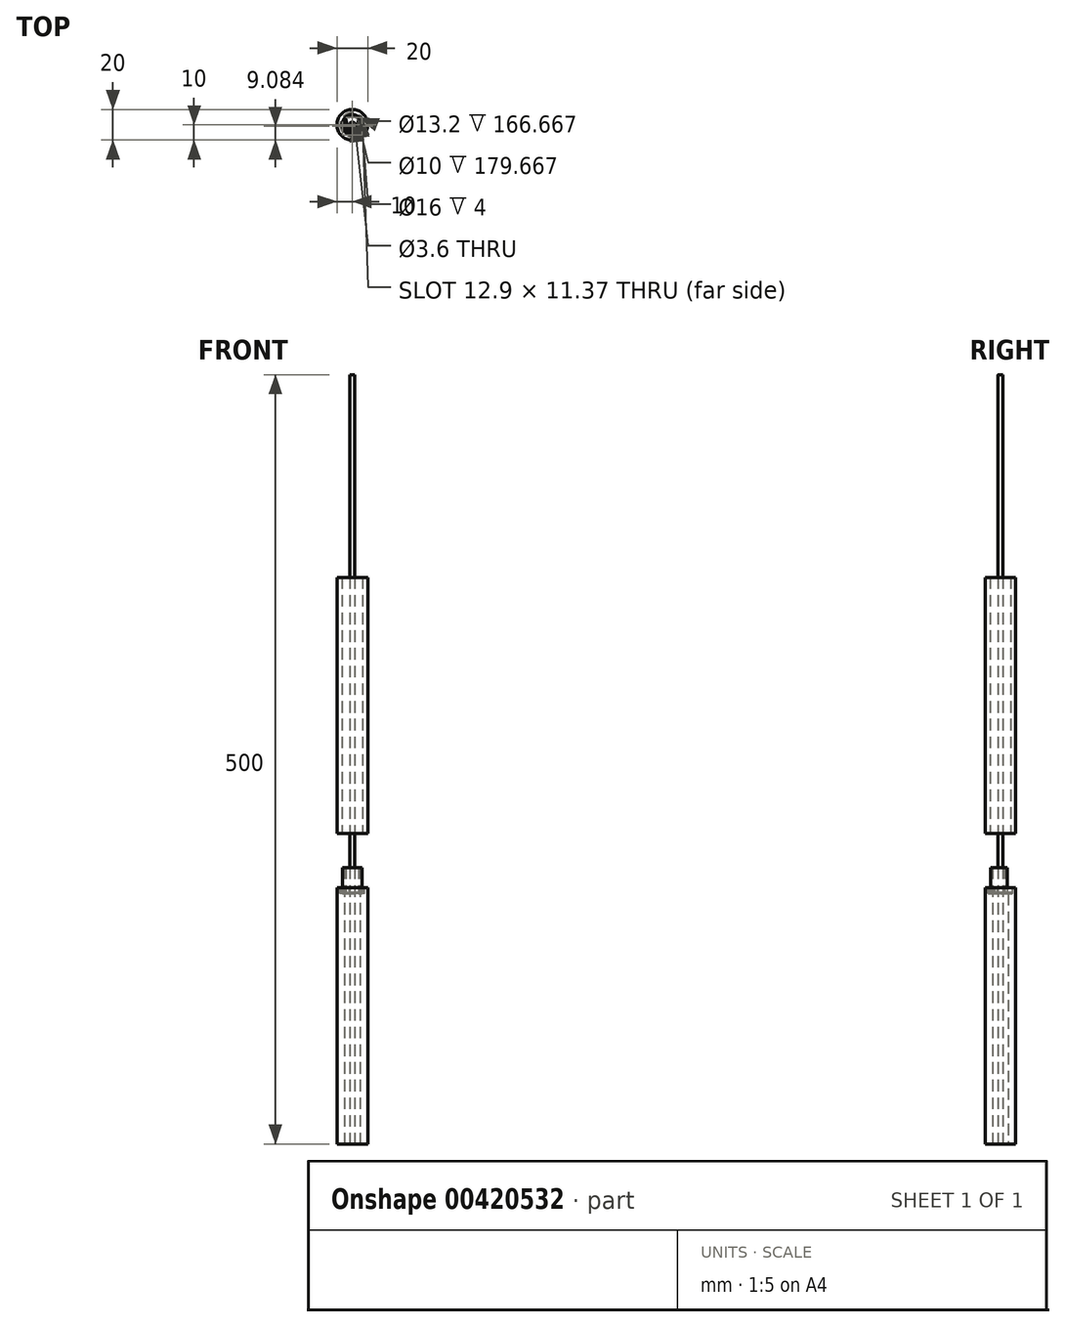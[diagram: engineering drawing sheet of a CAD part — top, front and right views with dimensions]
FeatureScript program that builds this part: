
annotation { "Feature Type Name" : "Feature", "Feature Type Description" : "" }
export const myFeature = defineFeature(function(context is Context, id is Id, definition is map)
    precondition{}
    {
        {
            assignVariable(context, id + "F0", {"name" : "RodLength", "anyValue" : 500 * mm});
        }
        {
            assignVariable(context, id + "F1", {"name" : "NubDepth", "anyValue" : 13 * mm});
        }
        {
            assignVariable(context, id + "F2", {"name" : "EjectorSupportRingDepth", "anyValue" : 3.2 * mm});
        }
        {
            var Q0;
            Q0=qCreatedBy(makeId("Top.planeOp"),FACE);
            cPlane(context, id + "F3", {"entities" : qUnion([Q0]), "cplaneType" : CPlaneType.OFFSET, "offset" : getVariable(context, 'RodLength') / 3, "width" : 150 * mm, "height" : 150 * mm});
        }
        {
            var Q0;
            Q0=qCreatedBy(id+"F3.planeOp",FACE);
            var sketch = newSketch(context, id + "F4", { "sketchPlane" : qUnion([Q0])});
            skArc(sketch, "E0", {"start": v(-4.56, 4.77) * mm, "mid": v(0, -6.6) * mm, "end": v(4.56, 4.77) * mm});
            skCircle(sketch, "E1", {"center": v(0, 0) * mm, "radius": 7.8 * mm});
            skCircle(sketch, "E2", {"center": v(0, 0) * mm, "radius": 1.8 * mm});
            skArc(sketch, "E3", {"start": v(-3.32, -0.75) * mm, "mid": v(0, -3.4) * mm, "end": v(3.32, -0.75) * mm});
            skLineSegment(sketch, "E4", {"start": v(-7.1, -0.75) * mm, "end": v(6.56, -0.75) * mm, "construction": true});
            skLineSegment(sketch, "E5", {"start": v(-3.32, -0.75) * mm, "end": v(-4.56, 4.77) * mm});
            skLineSegment(sketch, "E6", {"start": v(3.32, -0.75) * mm, "end": v(4.56, 4.77) * mm});
            skArc(sketch, "E7", {"start": v(-4.12, 2.83) * mm, "mid": v(0, -5) * mm, "end": v(4.12, 2.83) * mm});
            skPoint(sketch, "E8", {"position": v(-4.12, 2.83) * mm});
            skLineSegment(sketch, "E9", {"start": v(-4.12, 2.83) * mm, "end": v(-4.12, -8.26) * mm, "construction": true});
            skPoint(sketch, "E10", {"position": v(-4.12, -2.83) * mm});
            skArc(sketch, "E11", {"start": v(-4.51, 4.54) * mm, "mid": v(0, -6.4) * mm, "end": v(4.51, 4.54) * mm});
            skCircle(sketch, "E12", {"center": v(0, 0) * mm, "radius": 8 * mm});
            skSolve(sketch);
        }
        {
            var Q0;
            Q0=qCreatedBy(makeId("Top.planeOp"),FACE);
            var sketch = newSketch(context, id + "F5", { "sketchPlane" : qUnion([Q0])});
            skCircle(sketch, "E13", {"center": v(0, 0) * mm, "radius": 5 * mm});
            skCircle(sketch, "E14", {"center": v(0, 0) * mm, "radius": 10 * mm});
            skArc(sketch, "E15.0", {"start": v(-4.12, 2.83) * mm, "mid": v(0, -5) * mm, "end": v(4.12, 2.83) * mm});
            skSolve(sketch);
        }
        {
            var Q0;
            Q0=makeQuery(id+"F5.imprint","IMPRINT",FACE,{"disambiguationData":[TD([[makeQuery(id+"F5.imprint","IMPRINT",EDGE,{"derivedFrom":sQuery(id+"F5.wireOp",EDGE,"E13")}),-1.0]])]});
            var Q1;
            Q1=makeQuery(id+"F5.imprint","IMPRINT",FACE,{"disambiguationData":[TD([[makeQuery(id+"F5.imprint","IMPRINT",EDGE,{"derivedFrom":sQuery(id+"F5.wireOp",EDGE,"E13")}),1.0]])]});
            extrude(context, id + "F6", {"entities" : qUnion([Q0, Q1]), "depth" : getVariable(context, 'RodLength') / 3});
        }
        {
            var Q0;
            Q0=makeQuery(id+"F5.imprint","IMPRINT",FACE,{"disambiguationData":[TD([[makeQuery(id+"F5.imprint","IMPRINT",EDGE,{"derivedFrom":sQuery(id+"F5.wireOp",EDGE,"E13")}),1.0]])]});
            var Q1;
            Q1=qCreatedBy(id+"F3.planeOp",FACE);
            extrude(context, id + "F7", {"entities" : qUnion([Q0]), "operationType" : NewBodyOperationType.REMOVE, "endBound" : BoundingType.UP_TO_SURFACE, "endBoundEntityFace" : qUnion([Q1]), "depth" : getVariable(context, 'RodLength')});
        }
        {
            var Q0;
            {var subQ0=sQuery(id+"F4.wireOp",EDGE,"E7");Q0=makeQuery(id+"F4.imprint","IMPRINT",FACE,{"disambiguationData":[TD([[makeQuery(id+"F4.imprint","IMPRINT",EDGE,{"derivedFrom":subQ0}),-1.0]])]});}
            extrude(context, id + "F8", {"entities" : qUnion([Q0]), "operationType" : NewBodyOperationType.ADD, "depth" : getVariable(context, 'NubDepth')});
        }
        {
            var Q0;
            Q0=makeQuery(id+"F4.imprint","IMPRINT",FACE,{"disambiguationData":[TD([[makeQuery(id+"F4.imprint","IMPRINT",EDGE,{"derivedFrom":sQuery(id+"F4.wireOp",EDGE,"E0")}),-1.0]])]});
            var Q1;
            {var subQ0=sQuery(id+"F4.wireOp",EDGE,"E0");Q1=makeQuery(id+"F4.imprint","IMPRINT",FACE,{"disambiguationData":[TD([[makeQuery(id+"F4.imprint","IMPRINT",EDGE,{"derivedFrom":subQ0}),1.0]])]});}
            var Q2;
            Q2=makeQuery(id+"F4.imprint","IMPRINT",FACE,{"disambiguationData":[TD([[makeQuery(id+"F4.imprint","IMPRINT",EDGE,{"derivedFrom":sQuery(id+"F4.wireOp",EDGE,"E1")}),-1.0]])]});
            extrude(context, id + "F9", {"entities" : qUnion([Q0, Q1, Q2]), "operationType" : NewBodyOperationType.REMOVE, "oppositeDirection" : true, "depth" : getVariable(context, 'EjectorSupportRingDepth') + .8 * mm});
        }
        {
            var Q0;
            {var subQ1=sQuery(id+"F4.wireOp",EDGE,"E0");Q0=makeQuery(id+"F4.imprint","IMPRINT",FACE,{"disambiguationData":[TD([[makeQuery(id+"F4.imprint","IMPRINT",EDGE,{"derivedFrom":subQ1}),-1.0]])]});}
            extrude(context, id + "F10", {"entities" : qUnion([Q0]), "oppositeDirection" : true, "depth" : getVariable(context, 'EjectorSupportRingDepth')});
        }
        {
            var Q0;
            Q0=qCreatedBy(id+"F3.planeOp",FACE);
            cPlane(context, id + "F11", {"entities" : qUnion([Q0]), "cplaneType" : CPlaneType.OFFSET, "offset" : 35 * mm, "width" : 150 * mm, "height" : 150 * mm});
        }
        {
            var Q0;
            Q0=qCreatedBy(id+"F11.planeOp",FACE);
            var sketch = newSketch(context, id + "F12", { "sketchPlane" : qUnion([Q0])});
            skCircle(sketch, "E16.0", {"center": v(0, 0) * mm, "radius": 10 * mm});
            skCircle(sketch, "E17.converted", {"center": v(0, 0) * mm, "radius": 6.6 * mm});
            skPoint(sketch, "E18.orphan", {"position": v(-4.56, 4.77) * mm});
            skSolve(sketch);
        }
        {
            var Q0;
            Q0=makeQuery(id+"F12.imprint","IMPRINT",FACE,{"disambiguationData":[TD([[makeQuery(id+"F12.imprint","IMPRINT",EDGE,{"derivedFrom":sQuery(id+"F12.wireOp",EDGE,"E16.0")}),1.0]])]});
            extrude(context, id + "F13", {"entities" : qUnion([Q0]), "depth" : getVariable(context, 'RodLength') / 3});
        }
        {
            var Q0;
            Q0=qCreatedBy(makeId("Top.planeOp"),FACE);
            var sketch = newSketch(context, id + "F14", { "sketchPlane" : qUnion([Q0])});
            skCircle(sketch, "E19", {"center": v(0, 0) * mm, "radius": 1.58 * mm});
            skSolve(sketch);
        }
        {
            var Q0;
            Q0=makeQuery(id+"F14.imprint","IMPRINT",FACE,{"disambiguationData":[TD([[makeQuery(id+"F14.imprint","IMPRINT",EDGE,{"derivedFrom":sQuery(id+"F14.wireOp",EDGE,"E19")}),1.0]])]});
            extrude(context, id + "F15", {"entities" : qUnion([Q0]), "depth" : getVariable(context, 'RodLength')});
        }
    });
